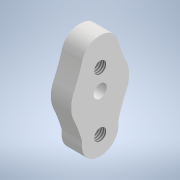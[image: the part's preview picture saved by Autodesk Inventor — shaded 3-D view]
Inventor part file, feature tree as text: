
AUTODESK INVENTOR PART (.ipt)
format: ipt  version: 2022 (Build 260153000, 153)  size: 173,568 bytes
history: native  units: mm
features: extrude x5, fillet x5, sketch x5, other x1, hole x1, projected_geometry x1
ambient origin geometry x8: Origin, YZ Plane, XZ Plane, XY Plane, X Axis, Y Axis, Z Axis, Center Point
bodies: Body1 (feature_tree)
feature tree (18):
  other  "ソリッド1"
  extrude  "押し出し1"  Depth=20.0mm
  extrude  "押し出し2"  Depth=7.0mm TaperAngle=0.0deg
  extrude  "押し出し3"  Depth=4.5mm
  fillet  "フィレット1"  [1 undecoded]
  hole  "穴1"  [1 undecoded]
  extrude  "押し出し4"  Depth=10.0mm TaperAngle=0.0deg
  fillet  "フィレット2"  Radius=50.0mm
  fillet  "フィレット3"  Radius=20.0mm
  extrude  "押し出し5"  Depth=7.0mm
  fillet  "フィレット4"  Radius=7.0mm
  fillet  "フィレット5"  Radius=6.0mm
  sketch  "スケッチ1"
  sketch  "スケッチ2"
  projected_geometry  "投影ループ1"
  sketch  "スケッチ4"
  sketch  "スケッチ6"
  sketch  "スケッチ7"
note: 2 required parameter values undecoded (feature->parameter linkage not recoverable at this tier; creation-order binding heuristic only, values carry confidence <= 0.55)
